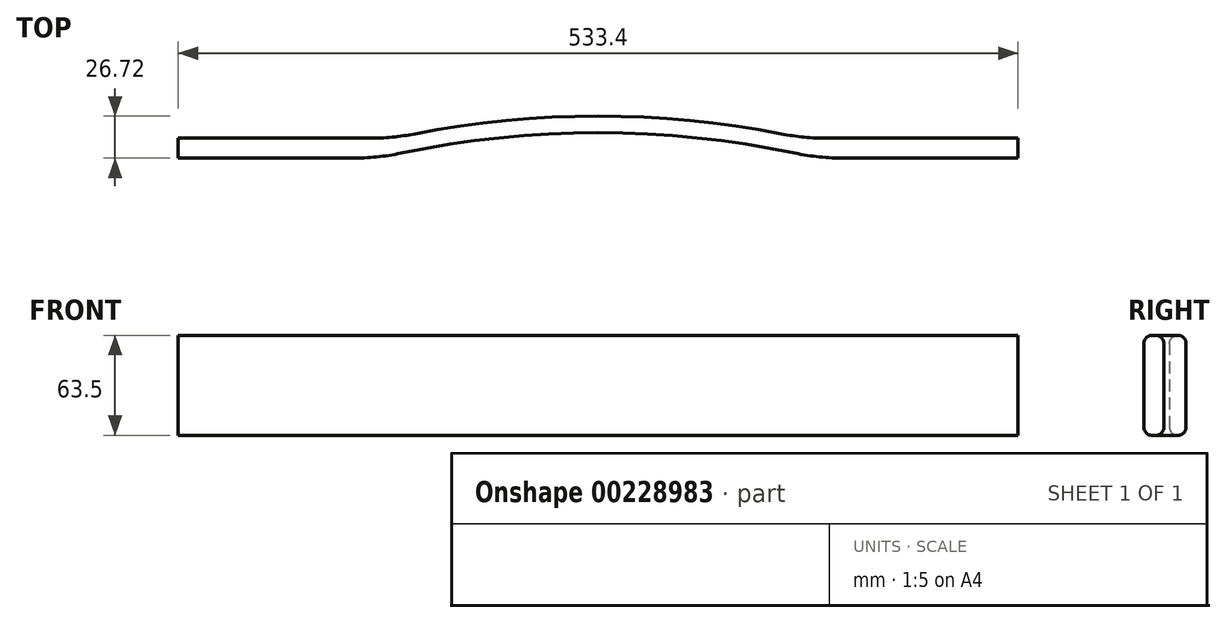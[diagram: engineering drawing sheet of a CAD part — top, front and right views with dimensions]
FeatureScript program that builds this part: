
annotation { "Feature Type Name" : "Feature", "Feature Type Description" : "" }
export const myFeature = defineFeature(function(context is Context, id is Id, definition is map)
    precondition{}
    {
        {
            var Q0;
            Q0=qCreatedBy(makeId("Top.planeOp"),FACE);
            var sketch = newSketch(context, id + "F0", { "sketchPlane" : qUnion([Q0])});
            skLineSegment(sketch, "E0.bottom", {"start": v(266.7, -6.35) * mm, "end": v(139.7, -6.35) * mm});
            skLineSegment(sketch, "E0.top", {"start": v(266.7, 6.35) * mm, "end": v(145.48, 6.35) * mm});
            skLineSegment(sketch, "E0.left", {"start": v(266.7, -6.35) * mm, "end": v(266.7, 6.35) * mm});
            skLineSegment(sketch, "E0.right", {"start": v(-266.7, -6.35) * mm, "end": v(-266.7, 6.35) * mm});
            skPoint(sketch, "E0.middle", {"position": v(0, 0) * mm});
            skLineSegment(sketch, "E1", {"start": v(139.7, 152.07) * mm, "end": v(-139.7, 152.07) * mm});
            skArc(sketch, "E2", {"start": v(116.38, 9.15) * mm, "mid": v(0, 20.37) * mm, "end": v(-116.38, 9.15) * mm});
            skArc(sketch, "E3", {"start": v(139.7, -6.35) * mm, "mid": v(0, 9.87) * mm, "end": v(-139.7, -6.35) * mm});
            skLineSegment(sketch, "E4.trimOffspring", {"start": v(-139.7, -6.35) * mm, "end": v(-266.7, -6.35) * mm});
            skLineSegment(sketch, "E5.trimOffspring", {"start": v(-145.48, 6.35) * mm, "end": v(-266.7, 6.35) * mm});
            skPoint(sketch, "E6.visualSharp", {"position": v(129.97, 6.35) * mm});
            skArc(sketch, "E6.filletArc", {"start": v(116.38, 9.15) * mm, "mid": v(130.86, 7.05) * mm, "end": v(145.48, 6.35) * mm});
            skPoint(sketch, "E7.visualSharp", {"position": v(-129.97, 6.35) * mm});
            skArc(sketch, "E7.filletArc", {"start": v(-145.48, 6.35) * mm, "mid": v(-130.86, 7.05) * mm, "end": v(-116.38, 9.15) * mm});
            skSolve(sketch);
        }
        {
            var Q0;
            Q0 = qSketchRegion(id + "F0", true);
            extrude(context, id + "F1", {"entities" : qUnion([Q0]), "depth" : 63.5 * mm});
        }
        {
            var Q0;
            Q0=makeQuery(id+"F1.opExtrude","SWEPT_EDGE",EDGE,{"disambiguationData":[OSD([sQuery(id+"F0.wireOp",EDGE,"E0.bottom"),sQuery(id+"F0.wireOp",EDGE,"E3")])]});
            var Q1;
            Q1=makeQuery(id+"F1.opExtrude","SWEPT_EDGE",EDGE,{"disambiguationData":[OSD([sQuery(id+"F0.wireOp",EDGE,"E3"),sQuery(id+"F0.wireOp",EDGE,"E4.trimOffspring")])]});
            fillet(context, id + "F2", {"entities" : qUnion([Q0, Q1]), "radius" : 152.4 * mm, "tangentPropagation" : true, "allowEdgeOverflow" : false});
        }
        {
            var Q0;
            Q0=makeQuery(id+"F1.opExtrude","CAP_EDGE",EDGE,{"disambiguationData":[OSD([sQuery(id+"F0.wireOp",EDGE,"E4.trimOffspring")])],"isStart":false});
            var Q1;
            Q1=makeQuery(id+"F1.opExtrude","CAP_EDGE",EDGE,{"disambiguationData":[OSD([sQuery(id+"F0.wireOp",EDGE,"E5.trimOffspring")])],"isStart":false});
            fillet(context, id + "F3", {"entities" : qUnion([Q0, Q1]), "radius" : 5.08 * mm, "tangentPropagation" : true, "allowEdgeOverflow" : false});
        }
        {
            var Q0;
            Q0=makeQuery(id+"F1.opExtrude","CAP_EDGE",EDGE,{"disambiguationData":[OSD([sQuery(id+"F0.wireOp",EDGE,"E5.trimOffspring")])],"isStart":true});
            var Q1;
            Q1=makeQuery(id+"F1.opExtrude","CAP_EDGE",EDGE,{"disambiguationData":[OSD([sQuery(id+"F0.wireOp",EDGE,"E4.trimOffspring")])],"isStart":true});
            fillet(context, id + "F4", {"entities" : qUnion([Q0, Q1]), "radius" : 5.08 * mm, "tangentPropagation" : true, "allowEdgeOverflow" : false});
        }
    });
